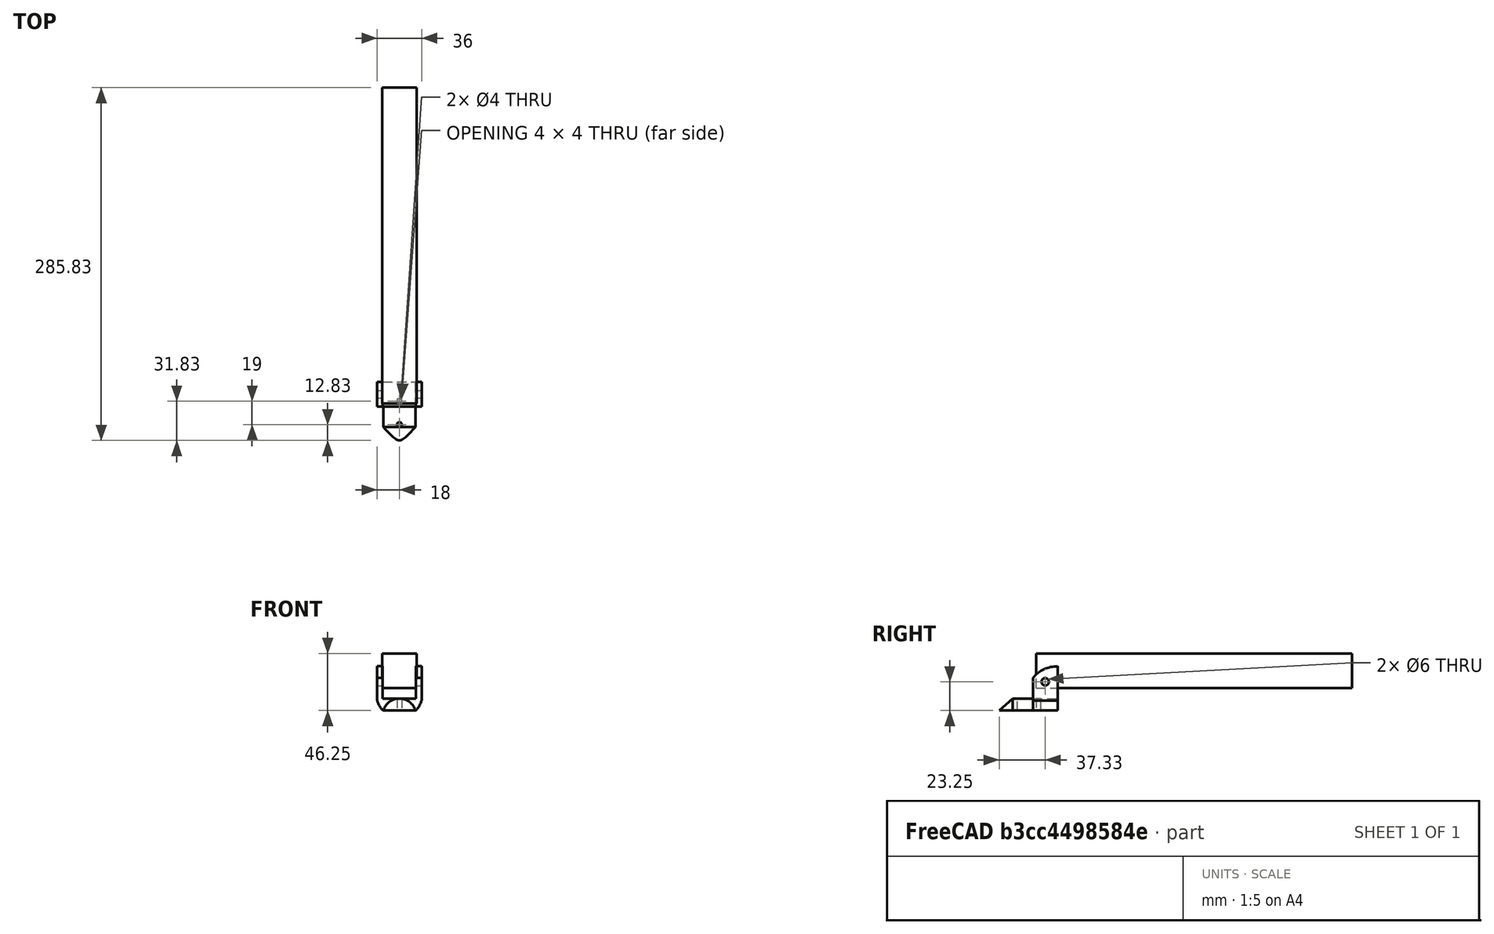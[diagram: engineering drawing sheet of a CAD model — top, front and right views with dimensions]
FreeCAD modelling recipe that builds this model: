
FCSTD DOCUMENT  (FreeCAD 0.20R29177 (Git))
Label: airModuleHolder07152022
License: All rights reserved
LicenseURL: http://en.wikipedia.org/wiki/All_rights_reserved
objects: Part::Cylinder×6, Part::Box×5, Part::MultiFuse×5, Part::Cut×4, Part::Cone×1, Part::MultiCommon×1
note: 22 computed .brp shape members not serialized (recipe doc carries the construction recipe); baked Part::Feature solids carry a one-line shape summary decoded from their .brp

FEATURE [Part::Cylinder] Cylinder
  Angle = 360
  AttacherType = Attacher::AttachEngine3D
  FirstAngle = 0
  Height = 19
  Placement = pos=(13.5,30,43) rot=(0,-0.707107,0.707107;3.14159rad)
  Radius = 13.5
  SecondAngle = 0
FEATURE [Part::Box] Box  label="TSlotFrameCut"
  AttacherType = Attacher::AttachEngine3D
  Height = 28
  Length = 28
  Placement = pos=(-0.5,30,65) rot=(0,0,1;0rad)
  Width = 256
FEATURE [Part::Box] Box015  label="TSlotMount001"
  AttacherType = Attacher::AttachEngine3D
  Height = 36
  Length = 36
  Placement = pos=(-4.5,27.5,46.75) rot=(0,0,1;0rad)
  Width = 20
FEATURE [Part::Cylinder] Cylinder009  label="m5Cut"
  Angle = 360
  AttacherType = Attacher::AttachEngine3D
  FirstAngle = 0
  Height = 100
  Placement = pos=(-56.4,37.5,70) rot=(0,1,0;1.5708rad)
  Radius = 3
  SecondAngle = 0
FEATURE [Part::Box] Box016  label="Shell_Holder002"
  AttacherType = Attacher::AttachEngine3D
  Height = 20
  Length = 27
  Placement = pos=(0,-20.5,26.75) rot=(0,0,1;0rad)
  Width = 75
FEATURE [Part::Cylinder] Cylinder011
  Angle = 360
  AttacherType = Attacher::AttachEngine3D
  FirstAngle = 0
  Height = 12
  Placement = pos=(13.5,32,45) rot=(0,0,1;1.5708rad)
  Radius = 2
  SecondAngle = 0
FEATURE [Part::Box] Box018  label="TSlotFrameCut001"
  AttacherType = Attacher::AttachEngine3D
  Height = 28.5
  Length = 27
  Placement = pos=(0,0,56.5) rot=(0,0,1;0rad)
  Width = 254
FEATURE [Part::Cut] Cut009  label="TSlotMount002"
  Base = -> Box015
  Tool = -> Box018
FEATURE [Part::Cylinder] Cylinder015
  Angle = 360
  AttacherType = Attacher::AttachEngine3D
  FirstAngle = 0
  Height = 12
  Placement = pos=(13.5,13,45) rot=(0,0,1;1.5708rad)
  Radius = 2
  SecondAngle = 0
FEATURE [Part::Cone] Cone
  Angle = 180
  AttacherType = Attacher::AttachEngine3D
  Height = 15
  Placement = pos=(13.5,11,43) rot=(1,0,0;1.5708rad)
  Radius1 = 13.5
  Radius2 = 0
FEATURE [Part::MultiFuse] Fusion  label="beak"
  Shapes = -> [Cylinder,Cone]
FEATURE [Part::Cut] Cut
  Base = -> Fusion
  Tool = -> Box016
FEATURE [Part::MultiFuse] Fusion001  label="heatSetCuts"
  Shapes = -> [Cylinder011,Cylinder015]
FEATURE [Part::Cut] Cut010
  Base = -> Cut009
  Tool = -> Cylinder009
FEATURE [Part::MultiFuse] Fusion002
  Shapes = -> [Cut,Cut010]
FEATURE [Part::Cut] Cut011  label="base"
  Base = -> Fusion002
  Tool = -> Fusion001
FEATURE [Part::Cylinder] Cylinder016  label="reshapes"
  Angle = 360
  AttacherType = Attacher::AttachEngine3D
  FirstAngle = 0
  Height = 66
  Placement = pos=(13.5,47.5,60) rot=(1,0,0;1.5708rad)
  Radius = 18.7
  SecondAngle = 0
FEATURE [Part::Box] Box019  label="reshapes001"
  AttacherType = Attacher::AttachEngine3D
  Height = 13
  Length = 40
  Placement = pos=(-6.5,27.5,60) rot=(0,0,1;0rad)
  Width = 20
FEATURE [Part::MultiFuse] Fusion003
  Shapes = -> [Box019,Cylinder016]
FEATURE [Part::Cylinder] Cylinder017
  Angle = 180
  AttacherType = Attacher::AttachEngine3D
  FirstAngle = 0
  Height = 38
  Placement = pos=(-6,47.5,56.6) rot=(-0.57735,-0.57735,-0.57735;4.18879rad)
  Radius = 26
  SecondAngle = 0
FEATURE [Part::MultiFuse] Fusion004
  Shapes = -> [Fusion003,Cylinder017]
FEATURE [Part::MultiCommon] Common  label="base001"
  Shapes = -> [Cut011,Fusion004]
